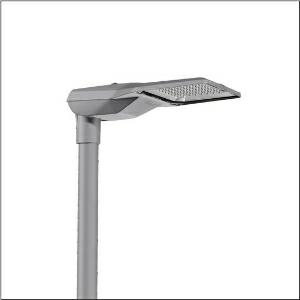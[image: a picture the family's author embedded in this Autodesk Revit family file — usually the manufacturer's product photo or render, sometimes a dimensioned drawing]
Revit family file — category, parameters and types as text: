
# Revit family: streetlight_sl_21_iq_midi___p0_5a_5xe3v31v08mb_f649
name_source: partatom
category: Lighting Fixtures
units: mm (PartAtom-declared; Revit-internal decimal feet)

## family parameters
Cut with Voids When Loaded = No
Host = Face
Light Source = No
Part Type = Normal
Room Calculation Point = No
Round Connector Dimension = Use Diameter
Shared = No

## types (1)
- --- (1 x LED, 18020 lm, 129.3 W, 3000K)
    Apparent Load = 129 VA
    CIE Flux Codes = 37 73 96 100 100
    Color Rendering = 70
    Color Temperature = 3000K
    Default Elevation = 1800 mm
    Description = Streetlight SL 21 iQ midi, mast luminaire, primary light control with lens, of PMMA, primary optical cover: cover, of toughened safety glass, transparent, light distribution: P0.5a, light emission: direct distribution, primary light characteristic: asymmetric, installation type: post-top, side-entry, LED, High Power LED, rated luminous flux: 18.020lm, luminous efficacy: 139lm/W, light colour: 730, colour temperature: 3000K, control gear: iQ-Street Remote, D4i with power reduction, control: pre-setting: logarithmic dimming characteristic, Street-Remote, Auto-Match, Temp-Guard, Lumen-Switch, Night-Set, Smart-Wire, Light-Fading, Desk-Remote (wireless, voltage-free reading and setting of iQ features in the workshop via application-optimized NFC function/RFID function), optimised constant luminous flux control (CLO 2.0), mains connection: 230..240V, AC, 50/60Hz, start of lifetime: 129W, end of service life: 142W, reduction: 56W, luminaire housing, of diecast aluminium, powder-coated, Siteco® metallic grey (DB 702S), corrosivity category C5 mid according to DIN EN ISO 12944, please order mast flange separately, inclination adjustable: 0°, 5°, 10°, 15°, sealing non-destructively replaceable, multi-level sealing system, length: 644mm, width: 335mm, height: 110mm, mast flange for spigot size: 42mm (side-entry): 5XC10008XM4, 60/48mm (side-entry/post-top): 5XC10108XM2, 76/60mm (side-entry/post-top): 5XC10108XM1, mounting height: 4..8m, Smart Interface above, protection rating (complete): IP66, insulation class (complete): insulation class II (safety insulation), certification: CE, ENEC, ENEC+, VDE, impact resistance: IK10, permissible operating ambient temperature for outdoor applications: -40..+50°C, standard-compliant lighting for roads and squares, packaging unit: 1 piece

Light Distribution: P0.5a
    Height = 111 mm
    Lamp = 1 x LED
    Lamp Light Flux = 18020 lm
    Lamp Power = 129.3 W
    Lamp count = 1
    Length = 644 mm
    Luminous efficacy = 139 lm/W
    Manufacturer = Siteco
    ModVariant = No
    Model = 5XE3V31V08MB
    Number of Poles = 1
    OnlyDefault = Yes
    Power Factor = 1
    Product Name = Streetlight SL 21 iQ midi | P0.5a
    Product group = mast luminaire | pylon top
    ProductGroupID = 6100
    Protection Class = Protection class II
    Protection Degree = IP 66
    RLX_Detail_Level = 1
    RLX_Emergency_Light_Flux = 0 lm
    RLX_Emergency_Type = 0
    RLX_Emergency_Type_DB = No
    RlxData = <blob elided: 90061 chars, md5=1e9d4343>
    Socket = socket
    Standby Power = 0 W
    System Light Flux = 18021 lm
    System Power = 129 W
    Type Comments = factory setting: luminous flux: 100 % | dim-lin: 254 | 672 mA
    Type Image = l_1004302.jpg
    URL = http://relux.com
    VarID = @adj_092003
    Voltage = 0 V
    Weight = 0.00 kg
    Width = 336 mm

## geometry (parser evidence)
native form markers: Blend x4, Sweep x9
no freeform markers — native parametric forms only
